# Revit family: PRD_AR_DspnsrsAndAccptncUnts_STRATOSHygieneBagDispenser_STR615
name_source: partatom
category: Specialty Equipment
units: mm (PartAtom-declared; Revit-internal decimal feet)

## family parameters
Cut with Voids When Loaded = No
Host = Face
OmniClass Number = 23.40.20.21
OmniClass Title = Toilet and Bath Specialties
Part Type = Normal
Room Calculation Point = No
Round Connector Dimension = Use Diameter
Shared = No

## types (1)
- STR615
    AssetType = Fixed
    BIMObjectName = PRD_AR_DispensersAndAcceptanceUnits_STRATOSHygieneBagDispenser_STR615
    Category = Pr_40_70_22, Dispensers and acceptance units
    Default Elevation = 900 mm  [stored 2.95276 ft]
    Description = STRATOS hygienic bag dispenser for wall mounting, stainless steel, surface satin finished, material thickness 1.2 mm, curved front with inspection window, incl. mounting material.
    DispenserMaterial = PRD_AR_StainlessSteel_SatinFinished
    DurationUnit = year
    Features = stainless steel, surface satin finished
    FillingQuantity = 100
    FillingQuantityUom = Pieces
    Finish = satin finished
    GrossWeight = 1.67 kg
    IfcExportAs = IfcFurnitureType
    IfcExportType = USERDEFINED
    IntegralAccessories = incl. stainless steel screws and dowels
    IsBuiltIn = TRUE
    Lock = No lock
    MainColor = stainless steel
    Manufacturer = KWC Group Management AG
    ManufacturerName = KWC Group Management AG
    ManufacturerURL = www.kwc-professional.com
    Material = stainless steel
    MaterialCode = 1.4301
    MaterialThickness = 1.50 mm
    Model = STR615
    ModelNumber = 3600008869
    ModelReference = STR615
    Name = STRATOS Hygiene Bag Dispenser STR615
    NetWeight = 1.44 kg
    NominalDepth = 90 mm  [stored 0.295276 ft]
    NominalHeight = 250 mm  [stored 0.82021 ft]
    NominalWidth = 156 mm  [stored 0.511811 ft]
    ProductInformation = http://pim.kwc.com
    Size = 156 x 250 x 90 mm
    Style = Hygiene bag dispenser
    TypeOfConsumable = Hygiene bag
    TypeOfFixing = Screw
    TypeOfMounting = Wall mounting
    TypeOfOperation = Manual operation
    URL = www.kwc-professional.com
    Uniclass2015Code = Pr_40_70_22
    Uniclass2015Title = Dispensers and acceptance units
    Uniclass2015Version = Products v1.10
    Version = 1
    WarrantyDurationUnit = year

note: [stored X ft] marks values corroborated as IEEE doubles in the binary element streams (Revit-internal decimal feet)

## geometry (parser evidence)
native form markers: Sweep x6
no freeform markers — native parametric forms only
